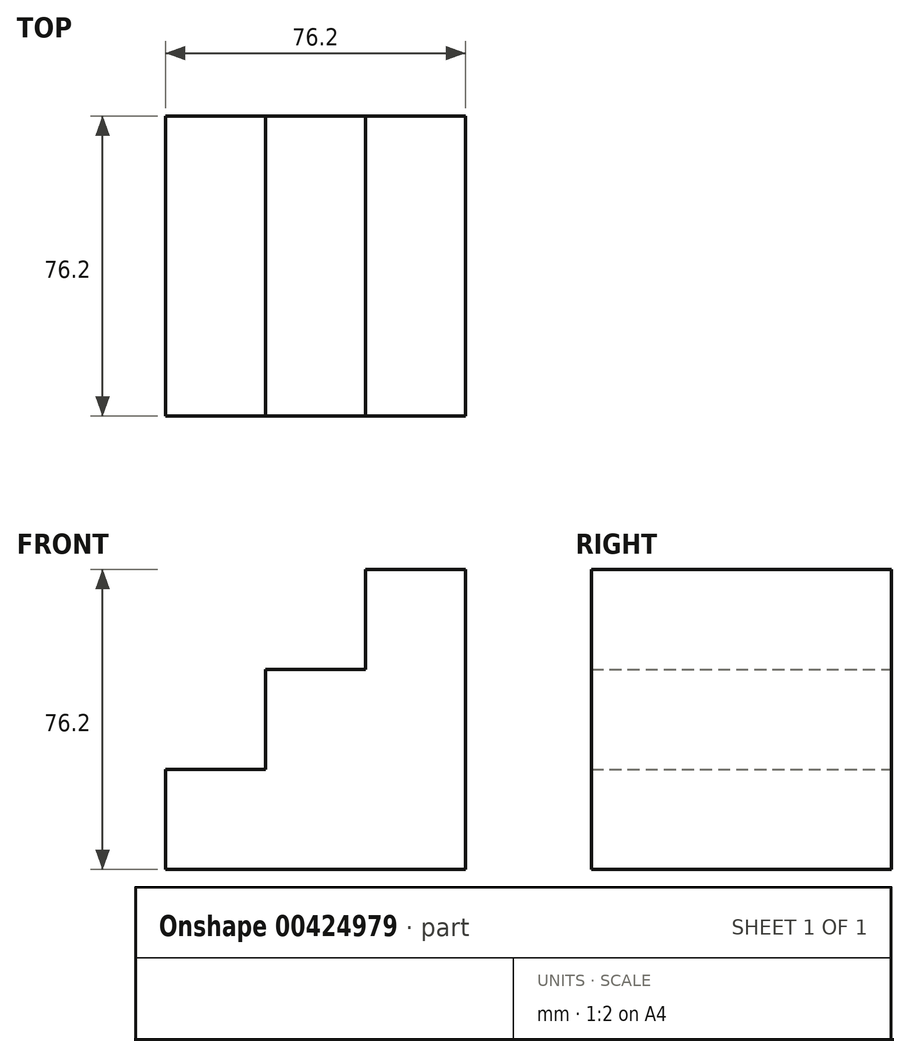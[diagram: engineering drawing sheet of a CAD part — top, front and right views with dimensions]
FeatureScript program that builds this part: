
annotation { "Feature Type Name" : "Feature", "Feature Type Description" : "" }
export const myFeature = defineFeature(function(context is Context, id is Id, definition is map)
    precondition{}
    {
        {
            var Q0;
            Q0=qCreatedBy(makeId("Front.planeOp"),FACE);
            var sketch = newSketch(context, id + "F0", { "sketchPlane" : qUnion([Q0])});
            skLineSegment(sketch, "E0", {"start": v(0, 0) * mm, "end": v(-76.2, 0) * mm});
            skLineSegment(sketch, "E1", {"start": v(-76.2, 0) * mm, "end": v(-76.2, 25.4) * mm});
            skLineSegment(sketch, "E2", {"start": v(-76.2, 25.4) * mm, "end": v(-50.8, 25.4) * mm});
            skLineSegment(sketch, "E3", {"start": v(-50.8, 25.4) * mm, "end": v(-50.8, 50.8) * mm});
            skLineSegment(sketch, "E4", {"start": v(-50.8, 50.8) * mm, "end": v(-25.4, 50.8) * mm});
            skLineSegment(sketch, "E5", {"start": v(-25.4, 50.8) * mm, "end": v(-25.4, 76.2) * mm});
            skLineSegment(sketch, "E6", {"start": v(-25.4, 76.2) * mm, "end": v(0, 76.2) * mm});
            skLineSegment(sketch, "E7", {"start": v(0, 76.2) * mm, "end": v(0, 0) * mm});
            skSolve(sketch);
        }
        {
            var Q0;
            Q0 = qSketchRegion(id + "F0", true);
            extrude(context, id + "F1", {"entities" : qUnion([Q0]), "depth" : 76.2 * mm});
        }
    });
